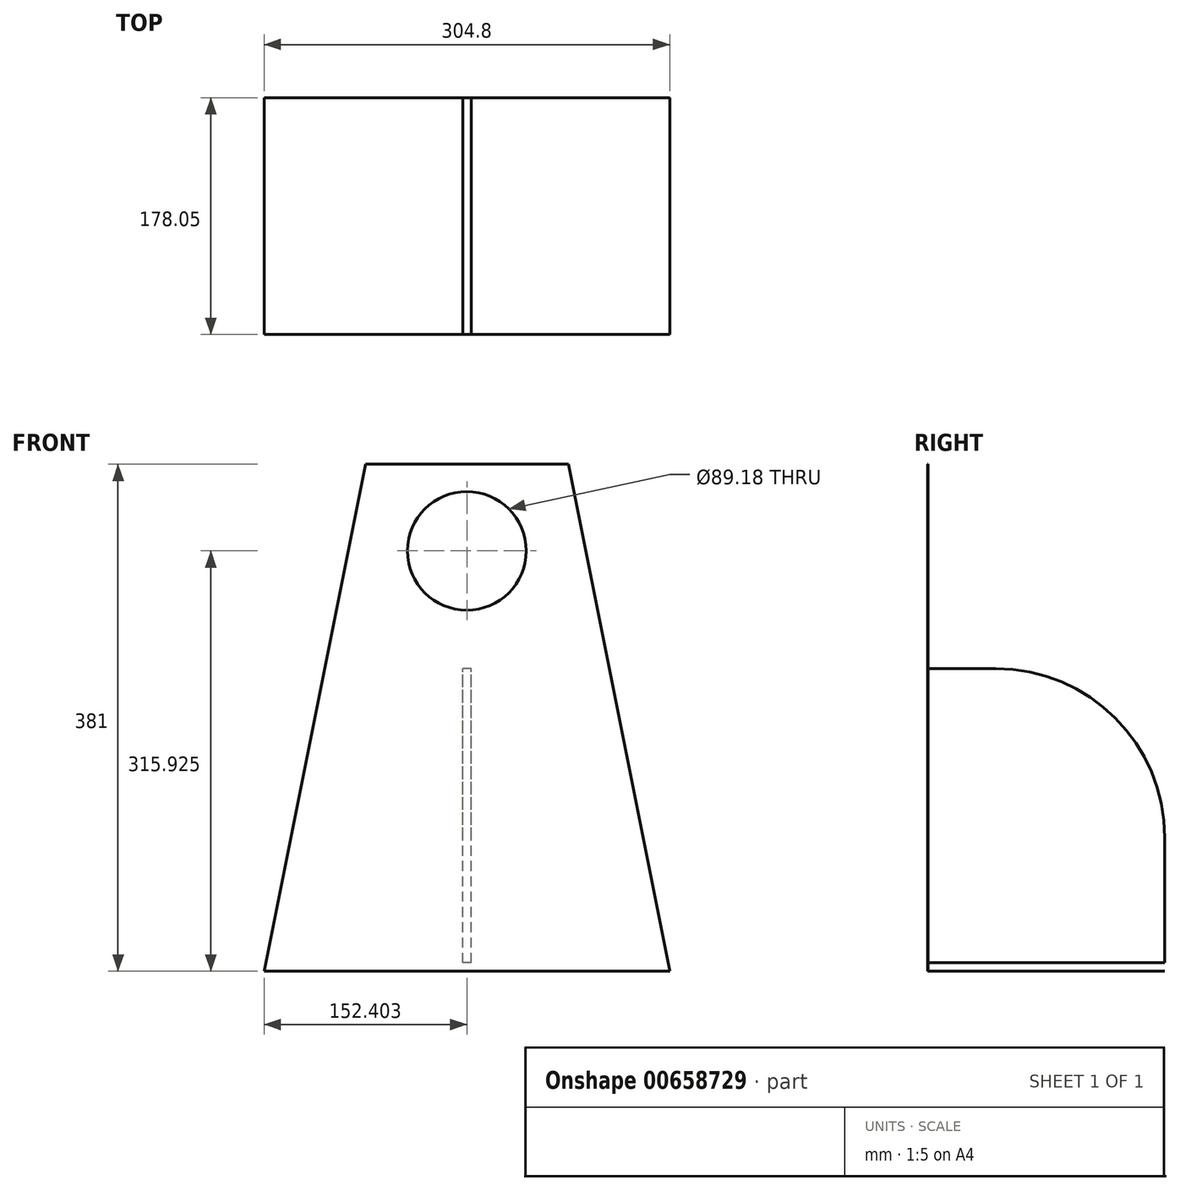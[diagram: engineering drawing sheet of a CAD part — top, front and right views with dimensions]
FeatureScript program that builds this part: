
annotation { "Feature Type Name" : "Feature", "Feature Type Description" : "" }
export const myFeature = defineFeature(function(context is Context, id is Id, definition is map)
    precondition{}
    {
        {
            assignVariable(context, id + "F0", {"name" : "w", "anyValue" : .25});
        }
        {
            var Q0;
            Q0=qCreatedBy(makeId("Front.planeOp"),FACE);
            var sketch = newSketch(context, id + "F1", { "sketchPlane" : qUnion([Q0])});
            skLineSegment(sketch, "E0", {"start": v(-22.64, 381) * mm, "end": v(-98.84, 0) * mm});
            skLineSegment(sketch, "E1", {"start": v(-98.84, 0) * mm, "end": v(205.96, 0) * mm});
            skLineSegment(sketch, "E2", {"start": v(205.96, 0) * mm, "end": v(129.76, 381) * mm});
            skLineSegment(sketch, "E3", {"start": v(-22.64, 381) * mm, "end": v(129.76, 381) * mm});
            skPoint(sketch, "E4", {"position": v(53.56, 381) * mm});
            skPoint(sketch, "E5", {"position": v(53.56, 0) * mm});
            skSolve(sketch);
        }
        {
            var Q0;
            Q0=qCreatedBy(makeId("Front.planeOp"),FACE);
            var sketch = newSketch(context, id + "F2", { "sketchPlane" : qUnion([Q0])});
            skCircle(sketch, "E6", {"center": v(53.56, 315.93) * mm, "radius": 44.59 * mm});
            skLineSegment(sketch, "E7.0.0", {"start": v(129.76, 381) * mm, "end": v(-22.64, 381) * mm});
            skLineSegment(sketch, "E7.0.1", {"start": v(-22.64, 381) * mm, "end": v(-98.84, 0) * mm});
            skLineSegment(sketch, "E7.0.2", {"start": v(-98.84, 0) * mm, "end": v(205.96, 0) * mm});
            skLineSegment(sketch, "E7.0.3", {"start": v(205.96, 0) * mm, "end": v(129.76, 381) * mm});
            skPoint(sketch, "E8", {"position": v(53.56, 381) * mm});
            skSolve(sketch);
        }
        {
            var Q0;
            Q0 = qSketchRegion(id + "F1", true);
            extrude(context, id + "F3", {"entities" : qUnion([Q0]), "depth" : (getVariable(context, 'w')) * mm, "offsetDistance" : 25.4 * mm});
        }
        {
            var Q0;
            Q0=sQuery(id+"F2.wireOp",VERTEX,"E6.center");
            var Q1;
            Q1=makeQuery(id+"F3.opExtrude","SWEPT_BODY",BODY,{"disambiguationData":[OSD([sQuery(id+"F1.wireOp",EDGE,"E0"),sQuery(id+"F1.wireOp",EDGE,"E1"),sQuery(id+"F1.wireOp",EDGE,"E2"),sQuery(id+"F1.wireOp",EDGE,"E3")])]});
            hole(context, id + "F4", {"style" : HoleStyle.SIMPLE, "endStyle" : HoleEndStyle.THROUGH, "oppositeDirection" : true, "holeDiameter" : 89.18 * mm, "majorDiameter" : 6.35 * mm, "isTappedThrough" : true, "tappedDepth" : 12.7 * mm, "tapClearance" : 3, "locations" : qUnion([Q0]), "scope" : qUnion([Q1])});
        }
        {
            var Q0;
            Q0=qCreatedBy(makeId("Top.planeOp"),FACE);
            var sketch = newSketch(context, id + "F5", { "sketchPlane" : qUnion([Q0])});
            skLineSegment(sketch, "E9.0", {"start": v(-98.84, 0) * mm, "end": v(205.96, 0) * mm});
            skLineSegment(sketch, "E10.top", {"start": v(-98.84, 177.8) * mm, "end": v(205.96, 177.8) * mm});
            skLineSegment(sketch, "E10.left", {"start": v(-98.84, 0) * mm, "end": v(-98.84, 177.8) * mm});
            skLineSegment(sketch, "E10.right", {"start": v(205.96, 0) * mm, "end": v(205.96, 177.8) * mm});
            skSolve(sketch);
        }
        {
            var Q0;
            Q0=makeQuery(id+"F5.imprint","IMPRINT",FACE,{"disambiguationData":[TD([[makeQuery(id+"F5.imprint","IMPRINT",EDGE,{"derivedFrom":sQuery(id+"F5.wireOp",EDGE,"E9.0")}),1.0]])]});
            extrude(context, id + "F6", {"entities" : qUnion([Q0]), "operationType" : NewBodyOperationType.ADD, "depth" : (getVariable(context, 'w')) * mm, "offsetDistance" : 25.4 * mm});
        }
        {
            var Q0;
            Q0=makeQuery(id+"F3.opExtrude","CAP_FACE",FACE,{"disambiguationData":[OSD([sQuery(id+"F1.wireOp",EDGE,"E0"),sQuery(id+"F1.wireOp",EDGE,"E1"),sQuery(id+"F1.wireOp",EDGE,"E2"),sQuery(id+"F1.wireOp",EDGE,"E3")])],"isStart":true});
            var sketch = newSketch(context, id + "F7", { "sketchPlane" : qUnion([Q0])});
            skLineSegment(sketch, "E11.1.0", {"start": v(-205.96, 6.35) * mm, "end": v(98.84, 6.35) * mm});
            skLineSegment(sketch, "E11.1.2", {"start": v(98.84, 6.35) * mm, "end": v(97.57, 6.35) * mm});
            skLineSegment(sketch, "E11.1.3", {"start": v(97.57, 6.35) * mm, "end": v(-204.7, 6.35) * mm});
            skLineSegment(sketch, "E11.1.4", {"start": v(-204.7, 6.35) * mm, "end": v(-205.96, 6.35) * mm});
            skLineSegment(sketch, "E12", {"start": v(-53.56, 6.35) * mm, "end": v(-53.56, 271.34) * mm});
            skLineSegment(sketch, "E13.bottom", {"start": v(-56.74, 6.35) * mm, "end": v(-50.39, 6.35) * mm});
            skLineSegment(sketch, "E13.top", {"start": v(-56.74, 227.46) * mm, "end": v(-50.39, 227.46) * mm});
            skLineSegment(sketch, "E13.left", {"start": v(-56.74, 6.35) * mm, "end": v(-56.74, 227.46) * mm});
            skLineSegment(sketch, "E13.right", {"start": v(-50.39, 6.35) * mm, "end": v(-50.39, 227.46) * mm});
            skPoint(sketch, "E14", {"position": v(-53.56, 227.46) * mm});
            skSolve(sketch);
        }
        {
            var Q0;
            Q0 = qSketchRegion(id + "F7", true);
            extrude(context, id + "F8", {"entities" : qUnion([Q0]), "operationType" : NewBodyOperationType.ADD, "depth" : 177.8 * mm, "offsetDistance" : 25.4 * mm});
        }
        {
            var Q0;
            Q0=makeQuery(id+"F8.opExtrude","CAP_EDGE",EDGE,{"disambiguationData":[OSD([sQuery(id+"F7.wireOp",EDGE,"E13.top")])],"isStart":false});
            fillet(context, id + "F9", {"entities" : qUnion([Q0]), "radius" : 127 * mm, "tangentPropagation" : true, "allowEdgeOverflow" : false});
        }
    });
